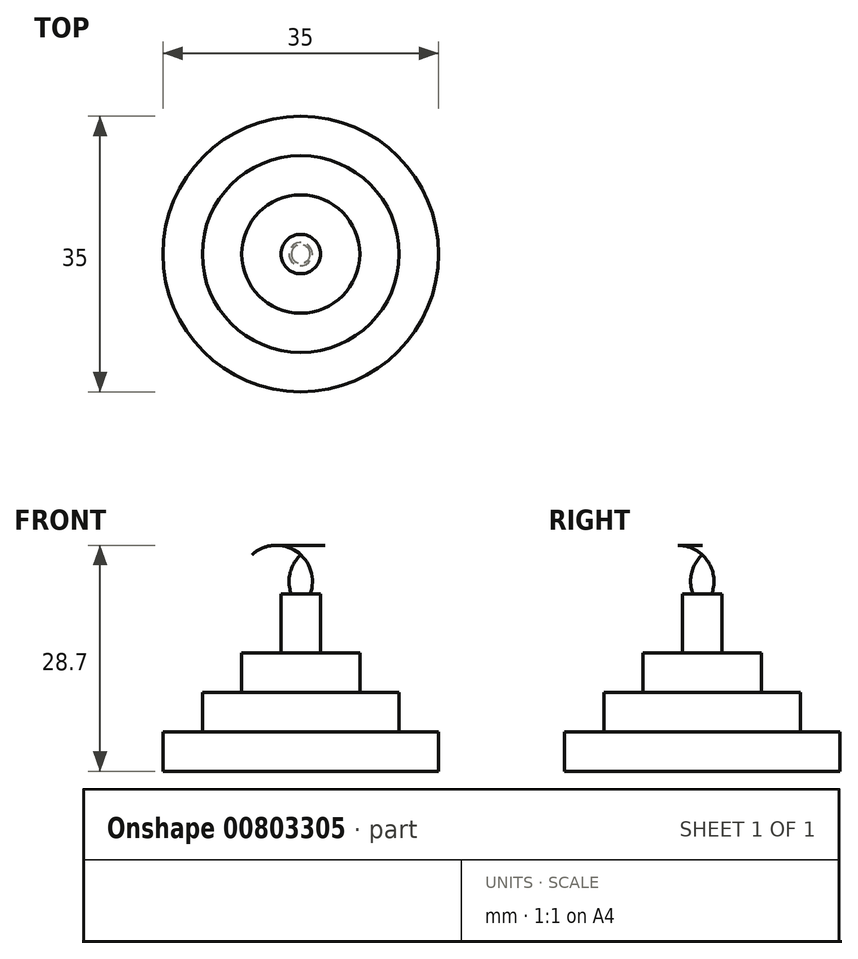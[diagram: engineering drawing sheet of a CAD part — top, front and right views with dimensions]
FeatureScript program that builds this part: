
annotation { "Feature Type Name" : "Feature", "Feature Type Description" : "" }
export const myFeature = defineFeature(function(context is Context, id is Id, definition is map)
    precondition{}
    {
        {
            var Q0;
            Q0=qCreatedBy(makeId("Front.planeOp"),FACE);
            var sketch = newSketch(context, id + "F0", { "sketchPlane" : qUnion([Q0])});
            skLineSegment(sketch, "E0", {"start": v(0, 0) * mm, "end": v(-17.5, 0) * mm});
            skLineSegment(sketch, "E1", {"start": v(-17.5, 0) * mm, "end": v(-17.5, 5) * mm});
            skLineSegment(sketch, "E2", {"start": v(-17.5, 5) * mm, "end": v(-12.5, 5) * mm});
            skLineSegment(sketch, "E3", {"start": v(-12.5, 5) * mm, "end": v(-12.5, 10) * mm});
            skLineSegment(sketch, "E4", {"start": v(-12.5, 10) * mm, "end": v(-7.5, 10) * mm});
            skLineSegment(sketch, "E5", {"start": v(-7.5, 10) * mm, "end": v(-7.5, 15) * mm});
            skLineSegment(sketch, "E6", {"start": v(-7.5, 15) * mm, "end": v(-2.5, 15) * mm});
            skLineSegment(sketch, "E7", {"start": v(-2.5, 15) * mm, "end": v(-2.5, 22.5) * mm});
            skLineSegment(sketch, "E8", {"start": v(-2.5, 22.5) * mm, "end": v(-1.2, 22.5) * mm});
            skArc(sketch, "E9", {"start": v(0, 27.5) * mm, "mid": v(-1.36, 25.18) * mm, "end": v(-1.2, 22.5) * mm});
            skLineSegment(sketch, "E10", {"start": v(0, 0) * mm, "end": v(0, 27.5) * mm});
            skLineSegment(sketch, "E11", {"start": v(0, -6.03) * mm, "end": v(0, 34.77) * mm, "construction": true});
            skSolve(sketch);
        }
        {
            var Q0;
            Q0 = qSketchRegion(id + "F0", true);
            var Q1;
            Q1=sQuery(id+"F0.wireOp",EDGE,"E11");
            revolve(context, id + "F1", {"surfaceOperationType" : NewSurfaceOperationType.NEW, "entities" : qUnion([Q0]), "axis" : qUnion([Q1]), "revolveType" : RevolveType.FULL});
        }
    });
